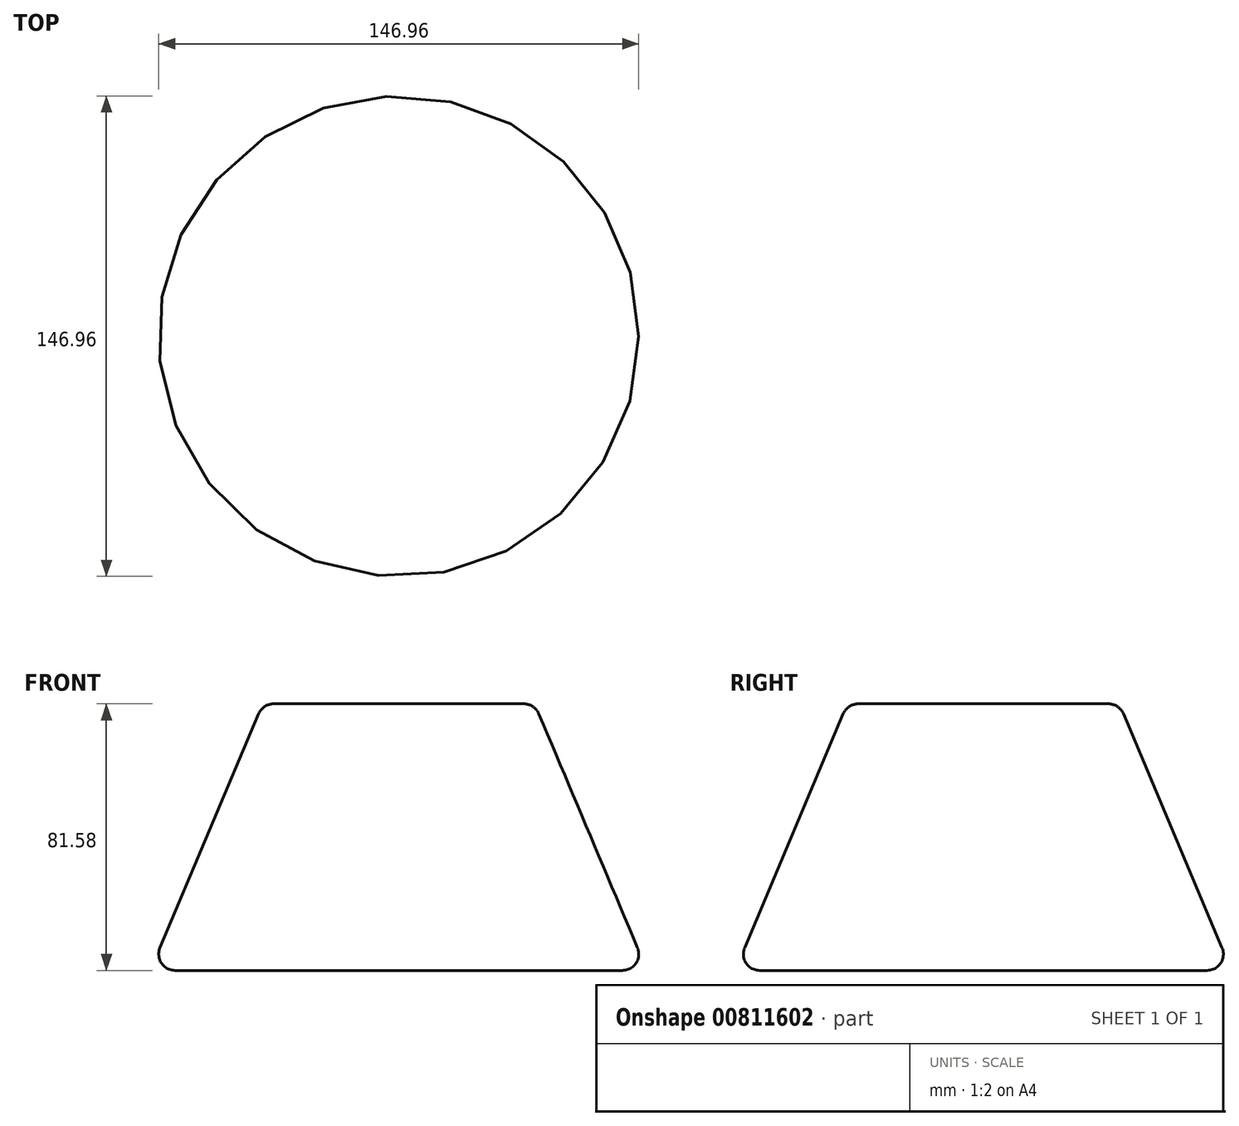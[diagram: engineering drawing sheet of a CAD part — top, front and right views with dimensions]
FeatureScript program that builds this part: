
annotation { "Feature Type Name" : "Feature", "Feature Type Description" : "" }
export const myFeature = defineFeature(function(context is Context, id is Id, definition is map)
    precondition{}
    {
        {
            var Q0;
            Q0=qCreatedBy(makeId("Front.planeOp"),FACE);
            var sketch = newSketch(context, id + "F0", { "sketchPlane" : qUnion([Q0])});
            skLineSegment(sketch, "E0", {"start": v(0, 0) * mm, "end": v(0, 81.58) * mm});
            skLineSegment(sketch, "E1", {"start": v(0, 81.58) * mm, "end": v(-41.58, 81.58) * mm});
            skLineSegment(sketch, "E2", {"start": v(-41.58, 81.58) * mm, "end": v(-76.01, 0) * mm});
            skLineSegment(sketch, "E3", {"start": v(-76.01, 0) * mm, "end": v(0, 0) * mm});
            skSolve(sketch);
        }
        {
            var Q0;
            Q0 = qSketchRegion(id + "F0", true);
            var Q1;
            Q1=sQuery(id+"F0.wireOp",EDGE,"E0");
            revolve(context, id + "F1", {"surfaceOperationType" : NewSurfaceOperationType.NEW, "entities" : qUnion([Q0]), "axis" : qUnion([Q1]), "revolveType" : RevolveType.FULL});
        }
        {
            var Q0;
            Q0=makeQuery(id+"F1.opRevolve","SWEPT_FACE",FACE,{"disambiguationData":[OSD([sQuery(id+"F0.wireOp",EDGE,"E3")])]});
            var Q1;
            Q1=makeQuery(id+"F1.opRevolve","SWEPT_EDGE",EDGE,{"disambiguationData":[OSD([sQuery(id+"F0.wireOp",EDGE,"E1"),sQuery(id+"F0.wireOp",EDGE,"E2")])]});
            fillet(context, id + "F2", {"entities" : qUnion([Q0, Q1]), "radius" : 5 * mm, "tangentPropagation" : true, "allowEdgeOverflow" : false});
        }
    });
